# Revit family: equip-water-cooler-elkay-vrc-hd
name_source: partatom
category: Plumbing Fixtures
units: mm (PartAtom-declared; Revit-internal decimal feet)

## family parameters
Always vertical = Yes
Cut with Voids When Loaded = No
OmniClass Number = 23.45.00.00
OmniClass Title = Sanitary, Laundry, and Cleaning Equipment
Part Type = Normal
Room Calculation Point = No
Round Connector Dimension = Use Radius
Shared = No
Work Plane-Based = No

## types (1)
- equip-water-cooler-elkay-vrc-hd
    Activation = VR Pushbutton
    Apparent Load Phase 1 = 0 VA
    Basin Material = Metal - Steel - Stainless - Chrome
    Bubbler = VR StreamSaver Bubbler
    CW Connection = Yes
    Cooler Depth = 1' - 6 9/16"
    Cooler Height = 1' - 8 7/16"
    Cooler Width = 3' - 0 1/2"
    Description = ADA Vandal Resistant Cooler
    Dispenser Height = 2' - 3"
    Filter = EWF172
    Glass Filter = -
    HW Connection = No
    Louver Screens = -
    Manufacturer = Elkay
    Model = LVRC8S
    Number of Poles = 1
    Orifice Height = 2' - 8 9/16"
    Other Features = VR pinned torx screws
    Panel Material = Metal - Steel - Stainless - Chrome
    Power Factor = 0
    Refrigerated = Yes
    Rim Height = 2' - 7 1/2"
    Sanitary Connector Description = Sanitary Connection
    Sanitary Service Radius = 0' - 0"
    Sanitary Service Size Radius = 0' - 0 5/8"
    Specification = http://www.elkayusa.com
    Type = Single
    URL = http://www.elkayusa.com
    Vent Connection = No
    Version = 1.0.0.0
    Volts/Hertz = 115V/60Hz
    Waste Connection = Yes
    Water Connector Description = Water Supply
    Water Service Flow = 0 GPM
    Water Service Size Radius = 0' - 0 1/4"

## geometry (parser evidence)
native form markers: Sweep x2
no freeform markers — native parametric forms only
